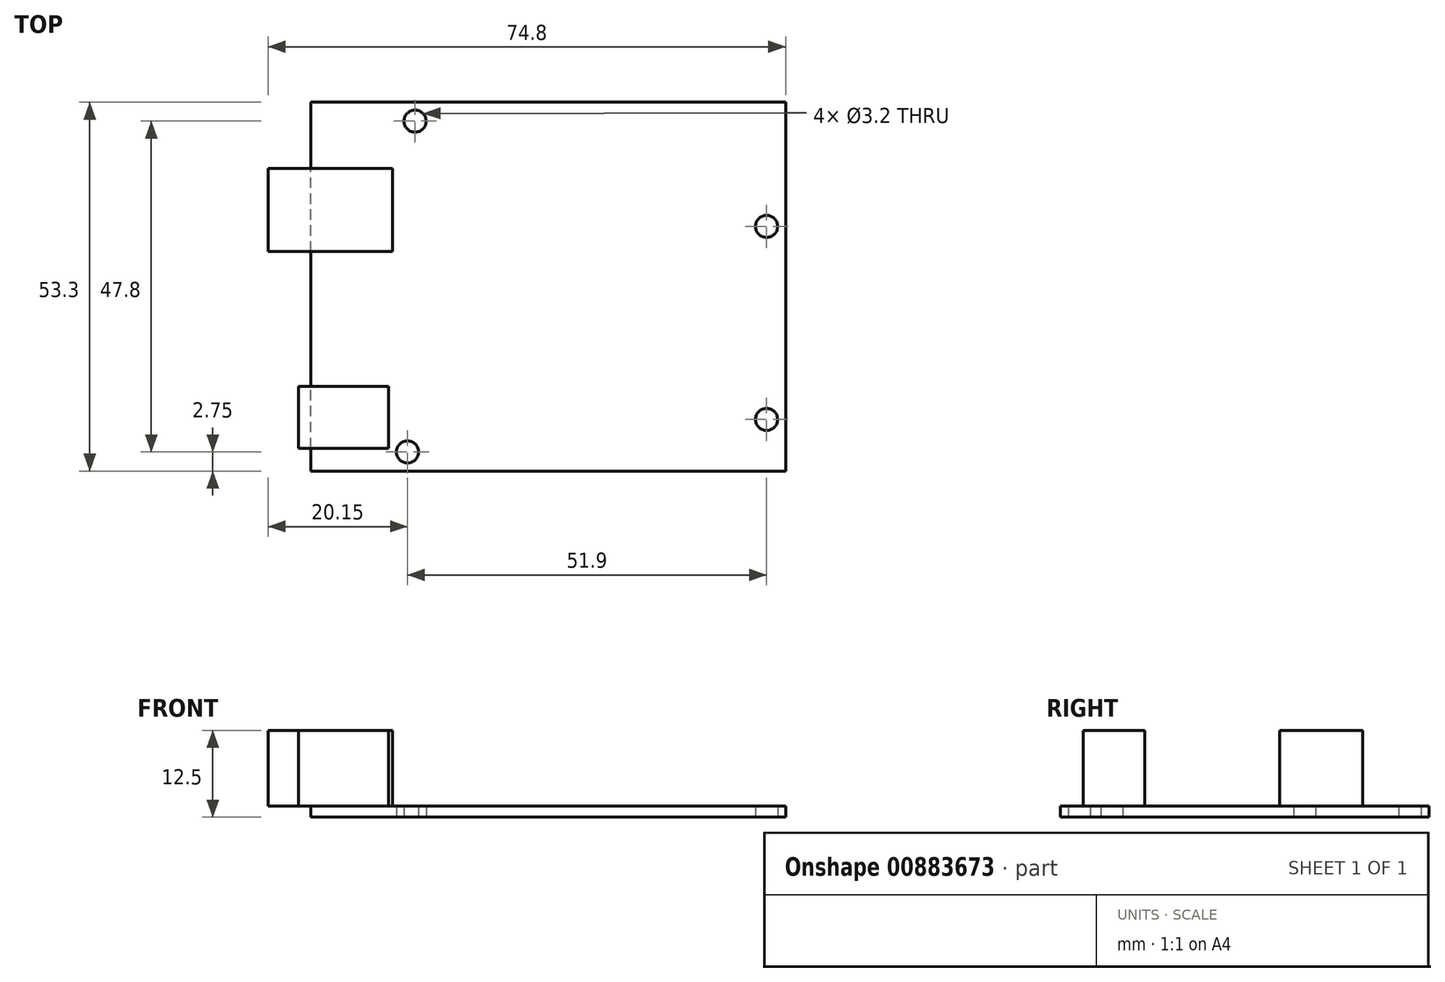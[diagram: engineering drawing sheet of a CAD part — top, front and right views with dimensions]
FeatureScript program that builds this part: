
annotation { "Feature Type Name" : "Feature", "Feature Type Description" : "" }
export const myFeature = defineFeature(function(context is Context, id is Id, definition is map)
    precondition{}
    {
        {
            var Q0;
            Q0=qCreatedBy(makeId("Top.planeOp"),FACE);
            var sketch = newSketch(context, id + "F0", { "sketchPlane" : qUnion([Q0])});
            skLineSegment(sketch, "E0.bottom", {"start": v(0, 0) * mm, "end": v(68.6, 0) * mm});
            skLineSegment(sketch, "E0.top", {"start": v(0, 53.3) * mm, "end": v(68.6, 53.3) * mm});
            skLineSegment(sketch, "E0.left", {"start": v(0, 0) * mm, "end": v(0, 53.3) * mm});
            skLineSegment(sketch, "E0.right", {"start": v(68.6, 0) * mm, "end": v(68.6, 53.3) * mm});
            skCircle(sketch, "E1", {"center": v(15.05, 50.55) * mm, "radius": 1.6 * mm});
            skCircle(sketch, "E2", {"center": v(13.95, 2.75) * mm, "radius": 1.6 * mm});
            skCircle(sketch, "E3", {"center": v(65.85, 35.35) * mm, "radius": 1.6 * mm});
            skCircle(sketch, "E4", {"center": v(65.85, 7.45) * mm, "radius": 1.6 * mm});
            skLineSegment(sketch, "E5", {"start": v(15.05, 50.55) * mm, "end": v(15.05, 53.3) * mm, "construction": true});
            skLineSegment(sketch, "E6", {"start": v(13.95, 2.75) * mm, "end": v(13.95, 0) * mm, "construction": true});
            skLineSegment(sketch, "E7", {"start": v(65.85, 35.35) * mm, "end": v(68.6, 35.35) * mm, "construction": true});
            skSolve(sketch);
        }
        {
            var Q0;
            Q0=makeQuery(id+"F0.imprint","IMPRINT",FACE,{"disambiguationData":[TD([[makeQuery(id+"F0.imprint","IMPRINT",EDGE,{"derivedFrom":sQuery(id+"F0.wireOp",EDGE,"E0.bottom")}),1.0]])]});
            extrude(context, id + "F1", {"entities" : qUnion([Q0]), "depth" : 1.6 * mm, "offsetDistance" : 25 * mm});
        }
        {
            var Q0;
            Q0=makeQuery(id+"F1.opExtrude","CAP_FACE",FACE,{"disambiguationData":[OSD([sQuery(id+"F0.wireOp",EDGE,"E0.bottom"),sQuery(id+"F0.wireOp",EDGE,"E0.top"),sQuery(id+"F0.wireOp",EDGE,"E0.left"),sQuery(id+"F0.wireOp",EDGE,"E0.right"),sQuery(id+"F0.wireOp",EDGE,"E1"),sQuery(id+"F0.wireOp",EDGE,"E2"),sQuery(id+"F0.wireOp",EDGE,"E3"),sQuery(id+"F0.wireOp",EDGE,"E4")])],"isStart":false});
            cPlane(context, id + "F2", {"entities" : qUnion([Q0]), "cplaneType" : CPlaneType.OFFSET, "offset" : 0 * mm, "width" : 150 * mm, "height" : 150 * mm});
        }
        {
            var Q0;
            Q0=qCreatedBy(id+"F2.planeOp",FACE);
            var sketch = newSketch(context, id + "F3", { "sketchPlane" : qUnion([Q0])});
            skLineSegment(sketch, "E8.bottom", {"start": v(-1.8, 3.3) * mm, "end": v(11.2, 3.3) * mm});
            skLineSegment(sketch, "E8.top", {"start": v(-1.8, 12.2) * mm, "end": v(11.2, 12.2) * mm});
            skLineSegment(sketch, "E8.left", {"start": v(-1.8, 3.3) * mm, "end": v(-1.8, 12.2) * mm});
            skLineSegment(sketch, "E8.right", {"start": v(11.2, 3.3) * mm, "end": v(11.2, 12.2) * mm});
            skLineSegment(sketch, "E9.bottom", {"start": v(-6.2, 31.7) * mm, "end": v(11.8, 31.7) * mm});
            skLineSegment(sketch, "E9.top", {"start": v(-6.2, 43.7) * mm, "end": v(11.8, 43.7) * mm});
            skLineSegment(sketch, "E9.left", {"start": v(-6.2, 31.7) * mm, "end": v(-6.2, 43.7) * mm});
            skLineSegment(sketch, "E9.right", {"start": v(11.8, 31.7) * mm, "end": v(11.8, 43.7) * mm});
            skSolve(sketch);
        }
        {
            var Q0;
            Q0 = qSketchRegion(id + "F3", true);
            extrude(context, id + "F4", {"entities" : qUnion([Q0]), "operationType" : NewBodyOperationType.ADD, "depth" : 10.9 * mm, "offsetDistance" : 25 * mm});
        }
    });
